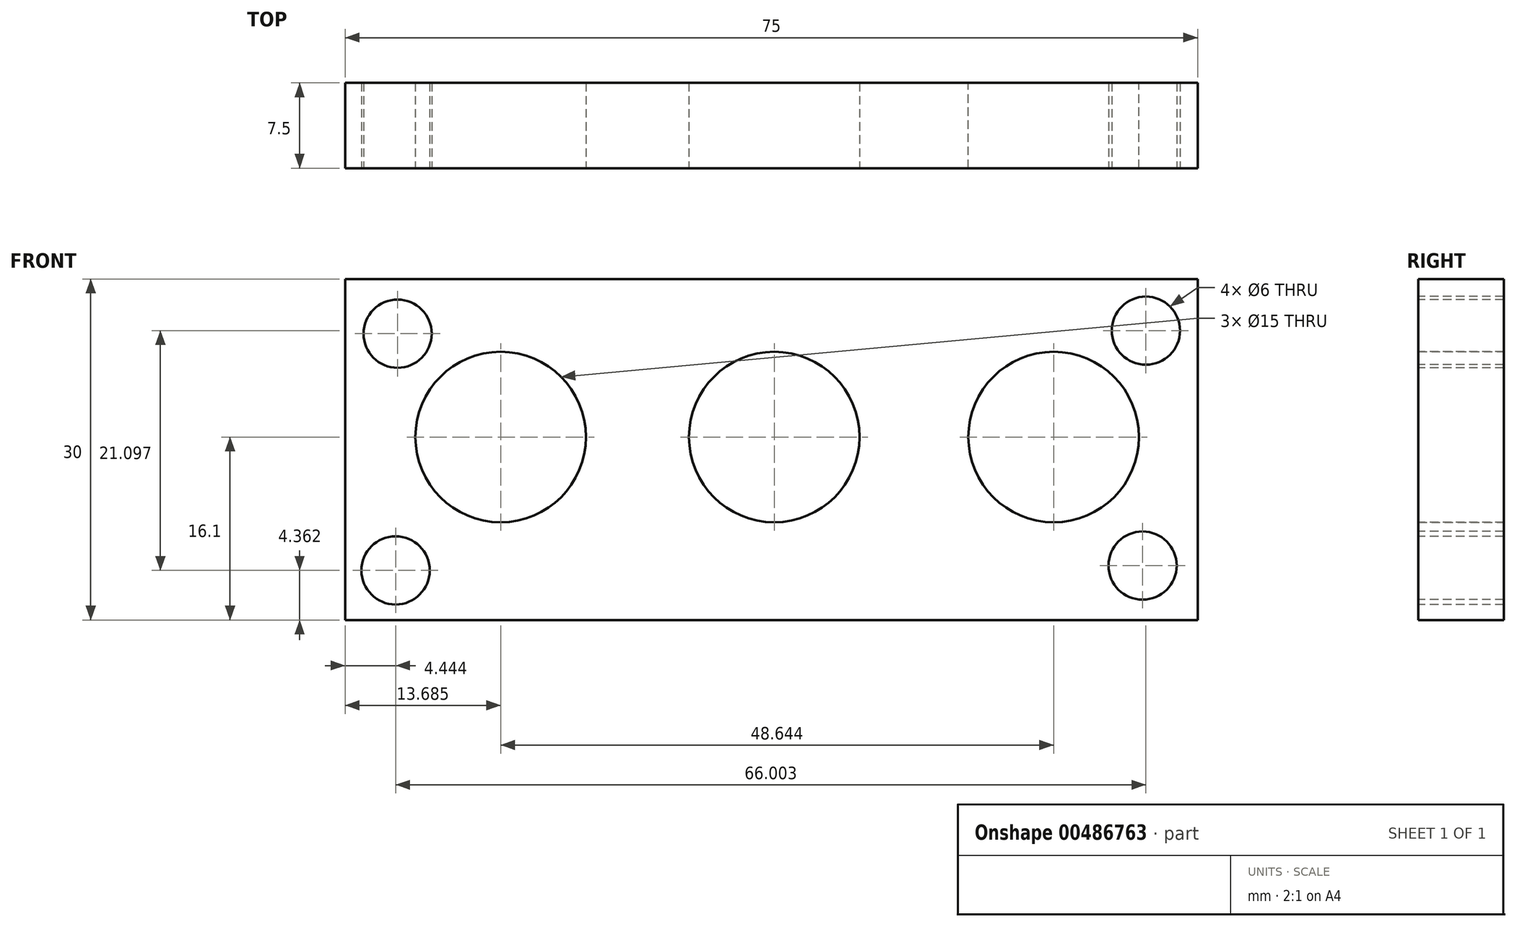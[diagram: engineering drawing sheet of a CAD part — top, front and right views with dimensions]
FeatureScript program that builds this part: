
annotation { "Feature Type Name" : "Feature", "Feature Type Description" : "" }
export const myFeature = defineFeature(function(context is Context, id is Id, definition is map)
    precondition{}
    {
        {
            var Q0;
            Q0=qCreatedBy(makeId("Front.planeOp"),FACE);
            var sketch = newSketch(context, id + "F0", { "sketchPlane" : qUnion([Q0])});
            skLineSegment(sketch, "E0.bottom", {"start": v(-41.52, 13.9) * mm, "end": v(33.48, 13.9) * mm});
            skLineSegment(sketch, "E0.top", {"start": v(-41.52, -16.1) * mm, "end": v(33.48, -16.1) * mm});
            skLineSegment(sketch, "E0.left", {"start": v(-41.52, 13.9) * mm, "end": v(-41.52, -16.1) * mm});
            skLineSegment(sketch, "E0.right", {"start": v(33.48, 13.9) * mm, "end": v(33.48, -16.1) * mm});
            skSolve(sketch);
        }
        {
            var Q0;
            Q0=makeQuery(id+"F0.imprint","IMPRINT",FACE,{"disambiguationData":[TD([[makeQuery(id+"F0.imprint","IMPRINT",EDGE,{"derivedFrom":sQuery(id+"F0.wireOp",EDGE,"E0.bottom")}),-1.0]])]});
            extrude(context, id + "F1", {"entities" : qUnion([Q0]), "depth" : 7.5 * mm});
        }
        {
            var Q0;
            Q0=makeQuery(id+"F1.opExtrude","CAP_FACE",FACE,{"disambiguationData":[OSD([sQuery(id+"F0.wireOp",EDGE,"E0.bottom"),sQuery(id+"F0.wireOp",EDGE,"E0.top"),sQuery(id+"F0.wireOp",EDGE,"E0.left"),sQuery(id+"F0.wireOp",EDGE,"E0.right")])],"isStart":true});
            var sketch = newSketch(context, id + "F2", { "sketchPlane" : qUnion([Q0])});
            skCircle(sketch, "E1", {"center": v(28.29, 0) * mm, "radius": 7.5 * mm});
            skCircle(sketch, "E2", {"center": v(3.36, 0) * mm, "radius": 7.5 * mm});
            skCircle(sketch, "E3", {"center": v(-20.8, 0) * mm, "radius": 7.5 * mm});
            skSolve(sketch);
        }
        {
            var Q0;
            Q0=makeQuery(id+"F2.imprint","IMPRINT",FACE,{"disambiguationData":[TD([[makeQuery(id+"F2.imprint","IMPRINT",EDGE,{"derivedFrom":sQuery(id+"F2.wireOp",EDGE,"E3")}),1.0]])]});
            extrude(context, id + "F3", {"entities" : qUnion([Q0]), "operationType" : NewBodyOperationType.REMOVE, "oppositeDirection" : true, "depth" : 25 * mm});
        }
        {
            var Q0;
            Q0=makeQuery(id+"F1.opExtrude","CAP_FACE",FACE,{"disambiguationData":[OSD([sQuery(id+"F0.wireOp",EDGE,"E0.bottom"),sQuery(id+"F0.wireOp",EDGE,"E0.top"),sQuery(id+"F0.wireOp",EDGE,"E0.left"),sQuery(id+"F0.wireOp",EDGE,"E0.right")])],"isStart":false});
            var sketch = newSketch(context, id + "F4", { "sketchPlane" : qUnion([Q0])});
            skCircle(sketch, "E4", {"center": v(-27.84, 0) * mm, "radius": 7.5 * mm});
            skCircle(sketch, "E5", {"center": v(-3.77, 0) * mm, "radius": 7.5 * mm});
            skSolve(sketch);
        }
        {
            var Q0;
            Q0=makeQuery(id+"F4.imprint","IMPRINT",FACE,{"disambiguationData":[TD([[makeQuery(id+"F4.imprint","IMPRINT",EDGE,{"derivedFrom":sQuery(id+"F4.wireOp",EDGE,"E5")}),1.0]])]});
            var Q1;
            Q1=makeQuery(id+"F4.imprint","IMPRINT",FACE,{"disambiguationData":[TD([[makeQuery(id+"F4.imprint","IMPRINT",EDGE,{"derivedFrom":sQuery(id+"F4.wireOp",EDGE,"E4")}),1.0]])]});
            extrude(context, id + "F5", {"entities" : qUnion([Q0, Q1]), "operationType" : NewBodyOperationType.REMOVE, "oppositeDirection" : true, "depth" : 25 * mm});
        }
        {
            var Q0;
            Q0=makeQuery(id+"F1.opExtrude","CAP_FACE",FACE,{"disambiguationData":[OSD([sQuery(id+"F0.wireOp",EDGE,"E0.bottom"),sQuery(id+"F0.wireOp",EDGE,"E0.top"),sQuery(id+"F0.wireOp",EDGE,"E0.left"),sQuery(id+"F0.wireOp",EDGE,"E0.right")])],"isStart":false});
            var sketch = newSketch(context, id + "F6", { "sketchPlane" : qUnion([Q0])});
            skCircle(sketch, "E6", {"center": v(-36.9, 9.09) * mm, "radius": 3 * mm});
            skCircle(sketch, "E7", {"center": v(-37.08, -11.74) * mm, "radius": 3 * mm});
            skCircle(sketch, "E8", {"center": v(28.93, 9.36) * mm, "radius": 3 * mm});
            skCircle(sketch, "E9", {"center": v(148.69, -16.1) * mm, "radius": 1.6 * mm});
            skCircle(sketch, "E10", {"center": v(28.63, -11.3) * mm, "radius": 3 * mm});
            skSolve(sketch);
        }
        {
            var Q0;
            Q0=makeQuery(id+"F6.imprint","IMPRINT",FACE,{"disambiguationData":[TD([[makeQuery(id+"F6.imprint","IMPRINT",EDGE,{"derivedFrom":sQuery(id+"F6.wireOp",EDGE,"E6")}),1.0]])]});
            var Q1;
            Q1=makeQuery(id+"F6.imprint","IMPRINT",FACE,{"disambiguationData":[TD([[makeQuery(id+"F6.imprint","IMPRINT",EDGE,{"derivedFrom":sQuery(id+"F6.wireOp",EDGE,"E7")}),1.0]])]});
            var Q2;
            Q2=makeQuery(id+"F6.imprint","IMPRINT",FACE,{"disambiguationData":[TD([[makeQuery(id+"F6.imprint","IMPRINT",EDGE,{"derivedFrom":sQuery(id+"F6.wireOp",EDGE,"E8")}),1.0]])]});
            var Q3;
            Q3=makeQuery(id+"F6.imprint","IMPRINT",FACE,{"disambiguationData":[TD([[makeQuery(id+"F6.imprint","IMPRINT",EDGE,{"derivedFrom":sQuery(id+"F6.wireOp",EDGE,"E10")}),1.0]])]});
            extrude(context, id + "F7", {"entities" : qUnion([Q0, Q1, Q2, Q3]), "operationType" : NewBodyOperationType.REMOVE, "endBound" : BoundingType.UP_TO_NEXT, "oppositeDirection" : true, "depth" : 25 * mm});
        }
    });
